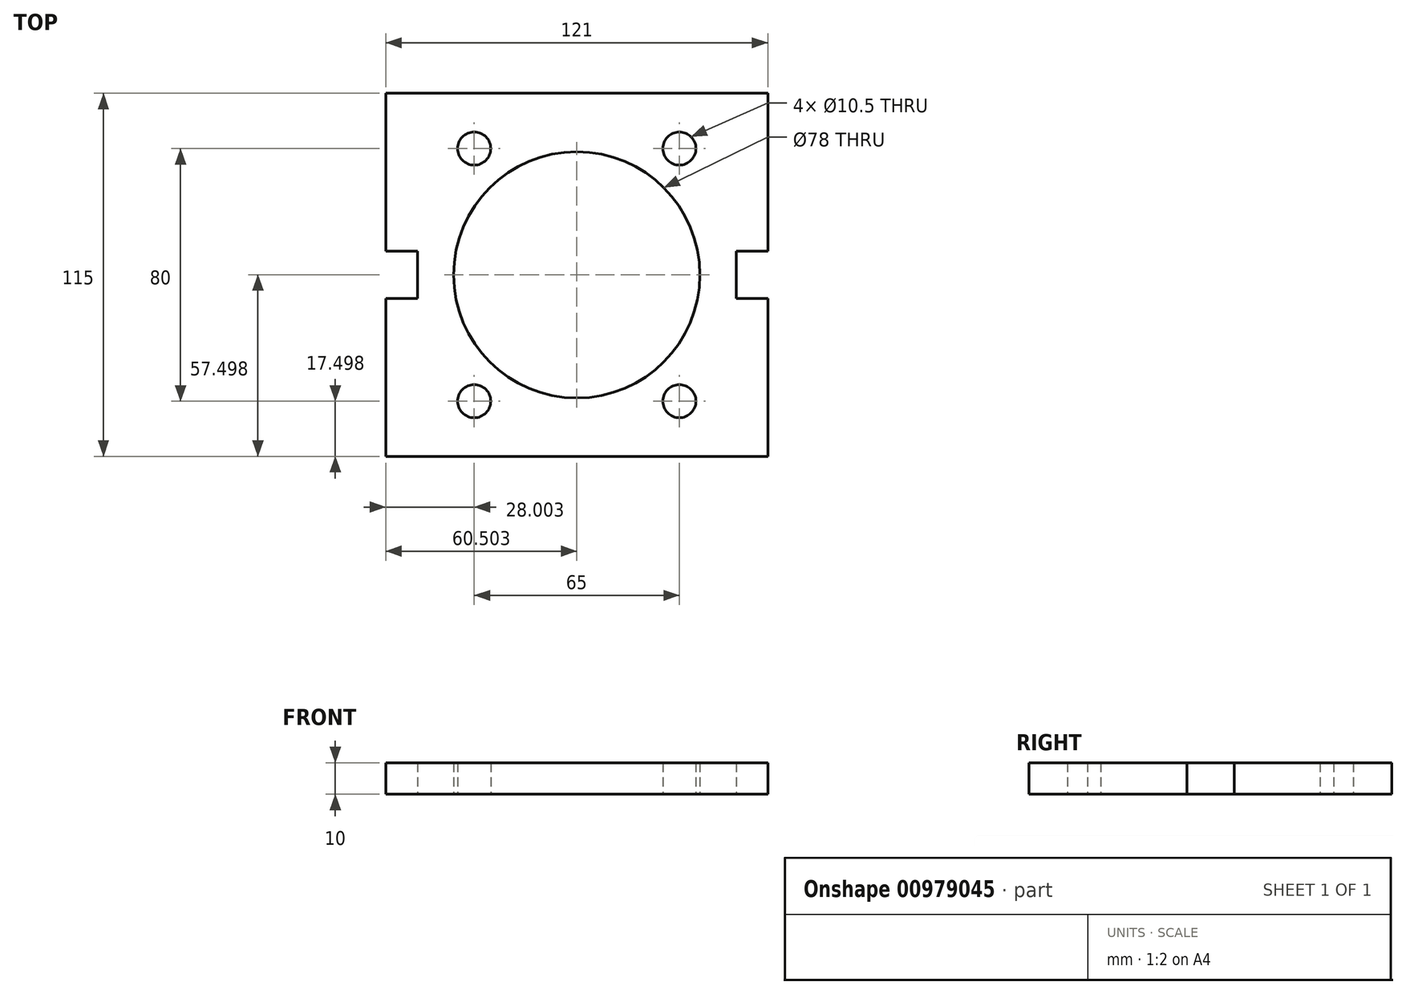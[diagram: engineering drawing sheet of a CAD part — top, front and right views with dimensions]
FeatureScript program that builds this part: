
annotation { "Feature Type Name" : "Feature", "Feature Type Description" : "" }
export const myFeature = defineFeature(function(context is Context, id is Id, definition is map)
    precondition{}
    {
        {
            var Q0;
            Q0=qCreatedBy(makeId("Top.planeOp"),FACE);
            var sketch = newSketch(context, id + "F0", { "sketchPlane" : qUnion([Q0])});
            skLineSegment(sketch, "E0.bottom", {"start": v(-64.94, 37.89) * mm, "end": v(56.06, 37.89) * mm});
            skLineSegment(sketch, "E0.top", {"start": v(-64.94, -77.11) * mm, "end": v(56.06, -77.11) * mm});
            skLineSegment(sketch, "E1", {"start": v(-64.94, 37.89) * mm, "end": v(-64.94, -12.11) * mm});
            skLineSegment(sketch, "E2", {"start": v(-64.94, -12.11) * mm, "end": v(-54.94, -12.11) * mm});
            skLineSegment(sketch, "E3", {"start": v(-54.94, -12.11) * mm, "end": v(-54.94, -27.11) * mm});
            skLineSegment(sketch, "E4", {"start": v(-54.94, -27.11) * mm, "end": v(-64.94, -27.11) * mm});
            skLineSegment(sketch, "E5", {"start": v(-64.94, -27.11) * mm, "end": v(-64.94, -77.11) * mm});
            skLineSegment(sketch, "E6", {"start": v(56.06, 37.89) * mm, "end": v(56.06, -12.11) * mm});
            skLineSegment(sketch, "E7", {"start": v(56.06, -12.11) * mm, "end": v(46.06, -12.11) * mm});
            skLineSegment(sketch, "E8", {"start": v(46.06, -12.11) * mm, "end": v(46.06, -27.11) * mm});
            skLineSegment(sketch, "E9", {"start": v(46.06, -27.11) * mm, "end": v(56.06, -27.11) * mm});
            skLineSegment(sketch, "E10", {"start": v(56.06, -27.11) * mm, "end": v(56.06, -77.11) * mm});
            skCircle(sketch, "E11", {"center": v(-4.44, -19.61) * mm, "radius": 39 * mm});
            skLineSegment(sketch, "E12.bottom", {"start": v(-36.94, 20.39) * mm, "end": v(28.06, 20.39) * mm});
            skLineSegment(sketch, "E12.top", {"start": v(-36.94, -59.61) * mm, "end": v(28.06, -59.61) * mm});
            skLineSegment(sketch, "E12.left", {"start": v(-36.94, 20.39) * mm, "end": v(-36.94, -59.61) * mm});
            skLineSegment(sketch, "E12.right", {"start": v(28.06, 20.39) * mm, "end": v(28.06, -59.61) * mm});
            skCircle(sketch, "E13", {"center": v(-36.94, 20.39) * mm, "radius": 5.25 * mm});
            skCircle(sketch, "E14", {"center": v(28.06, 20.39) * mm, "radius": 5.25 * mm});
            skCircle(sketch, "E15", {"center": v(-36.94, -59.61) * mm, "radius": 5.25 * mm});
            skCircle(sketch, "E16", {"center": v(28.06, -59.61) * mm, "radius": 5.25 * mm});
            skSolve(sketch);
        }
        {
            var Q0;
            Q0=makeQuery(id+"F0.imprint","IMPRINT",FACE,{"disambiguationData":[TD([[makeQuery(id+"F0.imprint","IMPRINT",EDGE,{"derivedFrom":sQuery(id+"F0.wireOp",EDGE,"E0.bottom")}),-1.0]])]});
            var Q1;
            {var subQ1=sQuery(id+"F0.wireOp",EDGE,"E11");var subQ9=sQuery(id+"F0.wireOp",EDGE,"E12.left");var subQ10=makeQuery(id+"F0.imprint","INTERSECT",VERTEX,{"disambiguationData":[OD(0.0)],"derivedFrom":[subQ1,subQ9]});Q1=makeQuery(id+"F0.imprint","IMPRINT",FACE,{"disambiguationData":[TD([[makeQuery(id+"F0.imprint","IMPRINT",EDGE,{"disambiguationData":[TD([[subQ10,1.0]])],"derivedFrom":subQ1}),-1.0]])]});}
            var Q2;
            {var subQ1=sQuery(id+"F0.wireOp",EDGE,"E11");var subQ5=sQuery(id+"F0.wireOp",EDGE,"E12.left");var subQ6=makeQuery(id+"F0.imprint","INTERSECT",VERTEX,{"disambiguationData":[OD(1.0)],"derivedFrom":[subQ1,subQ5]});Q2=makeQuery(id+"F0.imprint","IMPRINT",FACE,{"disambiguationData":[TD([[makeQuery(id+"F0.imprint","IMPRINT",EDGE,{"disambiguationData":[TD([[subQ6,-1.0]])],"derivedFrom":subQ1}),-1.0]])]});}
            extrude(context, id + "F1", {"entities" : qUnion([Q0, Q1, Q2]), "depth" : 10 * mm, "offsetDistance" : 25 * mm});
        }
    });
